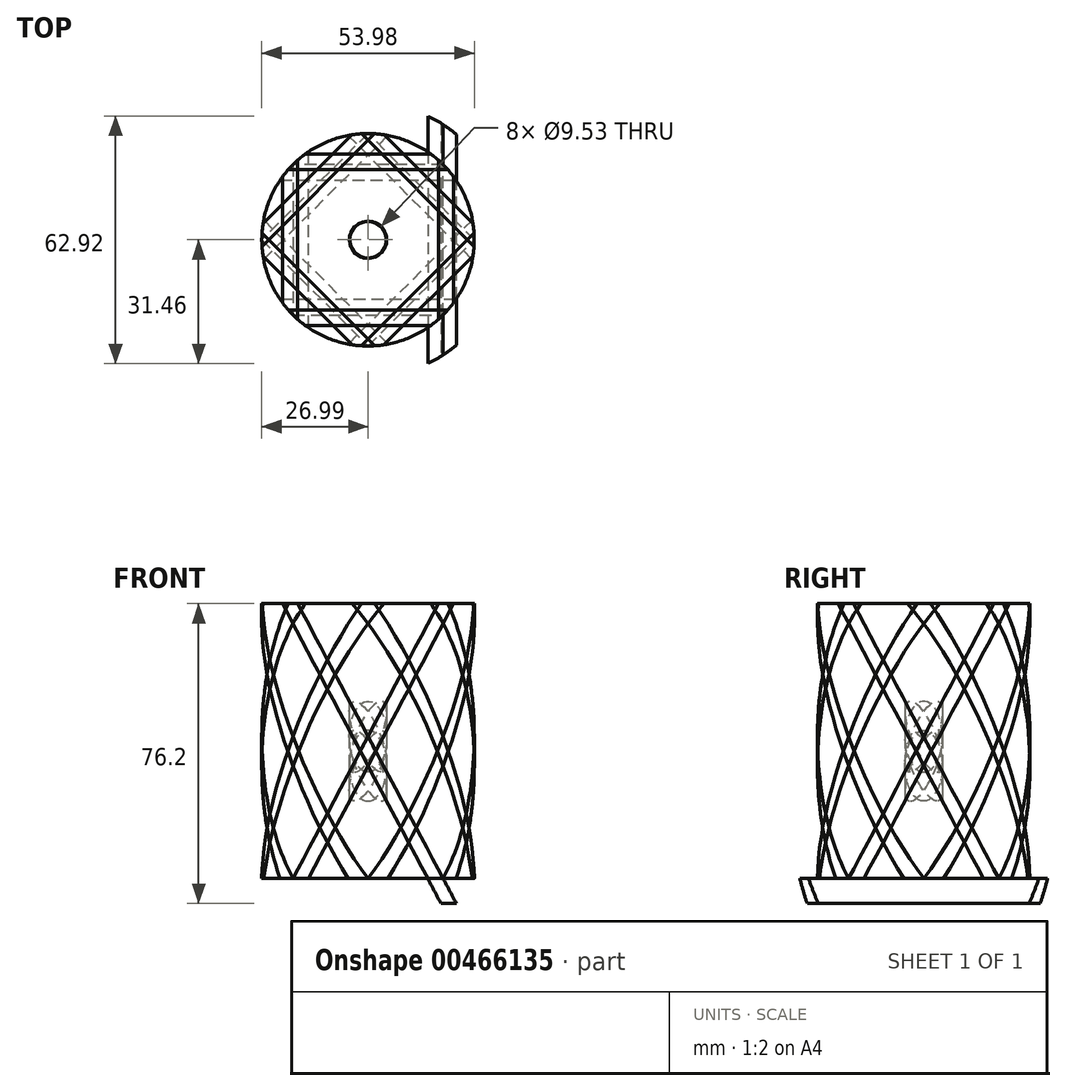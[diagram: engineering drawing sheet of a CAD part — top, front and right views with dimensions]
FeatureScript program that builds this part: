
annotation { "Feature Type Name" : "Feature", "Feature Type Description" : "" }
export const myFeature = defineFeature(function(context is Context, id is Id, definition is map)
    precondition{}
    {
        {
            var Q0;
            Q0=qCreatedBy(makeId("Top.planeOp"),FACE);
            var sketch = newSketch(context, id + "F0", { "sketchPlane" : qUnion([Q0])});
            skCircle(sketch, "E0", {"center": v(0, 0) * mm, "radius": 26.99 * mm});
            skCircle(sketch, "E1.0", {"center": v(0, 0) * mm, "radius": 20.64 * mm});
            skCircle(sketch, "E2", {"center": v(0, 0) * mm, "radius": 4.76 * mm});
            skCircle(sketch, "E3", {"center": v(0, 0) * mm, "radius": 34.93 * mm});
            skSolve(sketch);
        }
        {
            var Q0;
            Q0=qCreatedBy(makeId("Front.planeOp"),FACE);
            var sketch = newSketch(context, id + "F1", { "sketchPlane" : qUnion([Q0])});
            skLineSegment(sketch, "E4", {"start": v(-20.19, 74.24) * mm, "end": v(22.62, -6.7) * mm});
            skLineSegment(sketch, "E5", {"start": v(22.62, -6.7) * mm, "end": v(18.72, -6.7) * mm});
            skLineSegment(sketch, "E6", {"start": v(18.72, -6.7) * mm, "end": v(-24.1, 74.24) * mm});
            skLineSegment(sketch, "E7", {"start": v(-24.1, 74.24) * mm, "end": v(-20.19, 74.24) * mm});
            skLineSegment(sketch, "E8", {"start": v(0, 0) * mm, "end": v(0, 75.23) * mm, "construction": true});
            skSolve(sketch);
        }
        {
            var Q0;
            Q0=makeQuery(id+"F0.imprint","IMPRINT",FACE,{"disambiguationData":[TD([[makeQuery(id+"F0.imprint","IMPRINT",EDGE,{"derivedFrom":sQuery(id+"F0.wireOp",EDGE,"E0")}),-1.0]])]});
            var Q1;
            Q1=makeQuery(id+"F0.imprint","IMPRINT",FACE,{"disambiguationData":[TD([[makeQuery(id+"F0.imprint","IMPRINT",EDGE,{"derivedFrom":sQuery(id+"F0.wireOp",EDGE,"E0")}),1.0]])]});
            var Q2;
            Q2=makeQuery(id+"F0.imprint","IMPRINT",FACE,{"disambiguationData":[TD([[makeQuery(id+"F0.imprint","IMPRINT",EDGE,{"derivedFrom":sQuery(id+"F0.wireOp",EDGE,"E1.0")}),1.0]])]});
            extrude(context, id + "F2", {"entities" : qUnion([Q0, Q1, Q2]), "oppositeDirection" : true, "depth" : 6.35 * mm});
        }
        {
            var Q0;
            Q0=makeQuery(id+"F0.imprint","IMPRINT",FACE,{"disambiguationData":[TD([[makeQuery(id+"F0.imprint","IMPRINT",EDGE,{"derivedFrom":sQuery(id+"F0.wireOp",EDGE,"E1.0")}),1.0]])]});
            var Q1;
            Q1=makeQuery(id+"F0.imprint","IMPRINT",FACE,{"disambiguationData":[TD([[makeQuery(id+"F0.imprint","IMPRINT",EDGE,{"derivedFrom":sQuery(id+"F0.wireOp",EDGE,"E0")}),1.0]])]});
            extrude(context, id + "F3", {"entities" : qUnion([Q0, Q1]), "depth" : 69.85 * mm});
        }
        {
            var Q0;
            Q0=qSketchRegion(id+"F1",true);
            extrude(context, id + "F4", {"entities" : qUnion([Q0]), "operationType" : NewBodyOperationType.INTERSECT, "depth" : 101.6 * mm, "symmetric" : true});
        }
        {
            var Q0;
            Q0=makeQuery(id+"F3.opExtrude","SWEPT_BODY",BODY,{"disambiguationData":[OSD([sQuery(id+"F0.wireOp",EDGE,"E0"),sQuery(id+"F0.wireOp",EDGE,"E2")])]});
            var Q1;
            Q1=sQuery(id+"F1.wireOp",EDGE,"E8");
            circularPattern(context, id + "F5", {"entities" : qUnion([Q0]), "axis" : qUnion([Q1]), "angle" : 360 * degree, "instanceCount" : 8, "equalSpace" : true});
        }
    });
